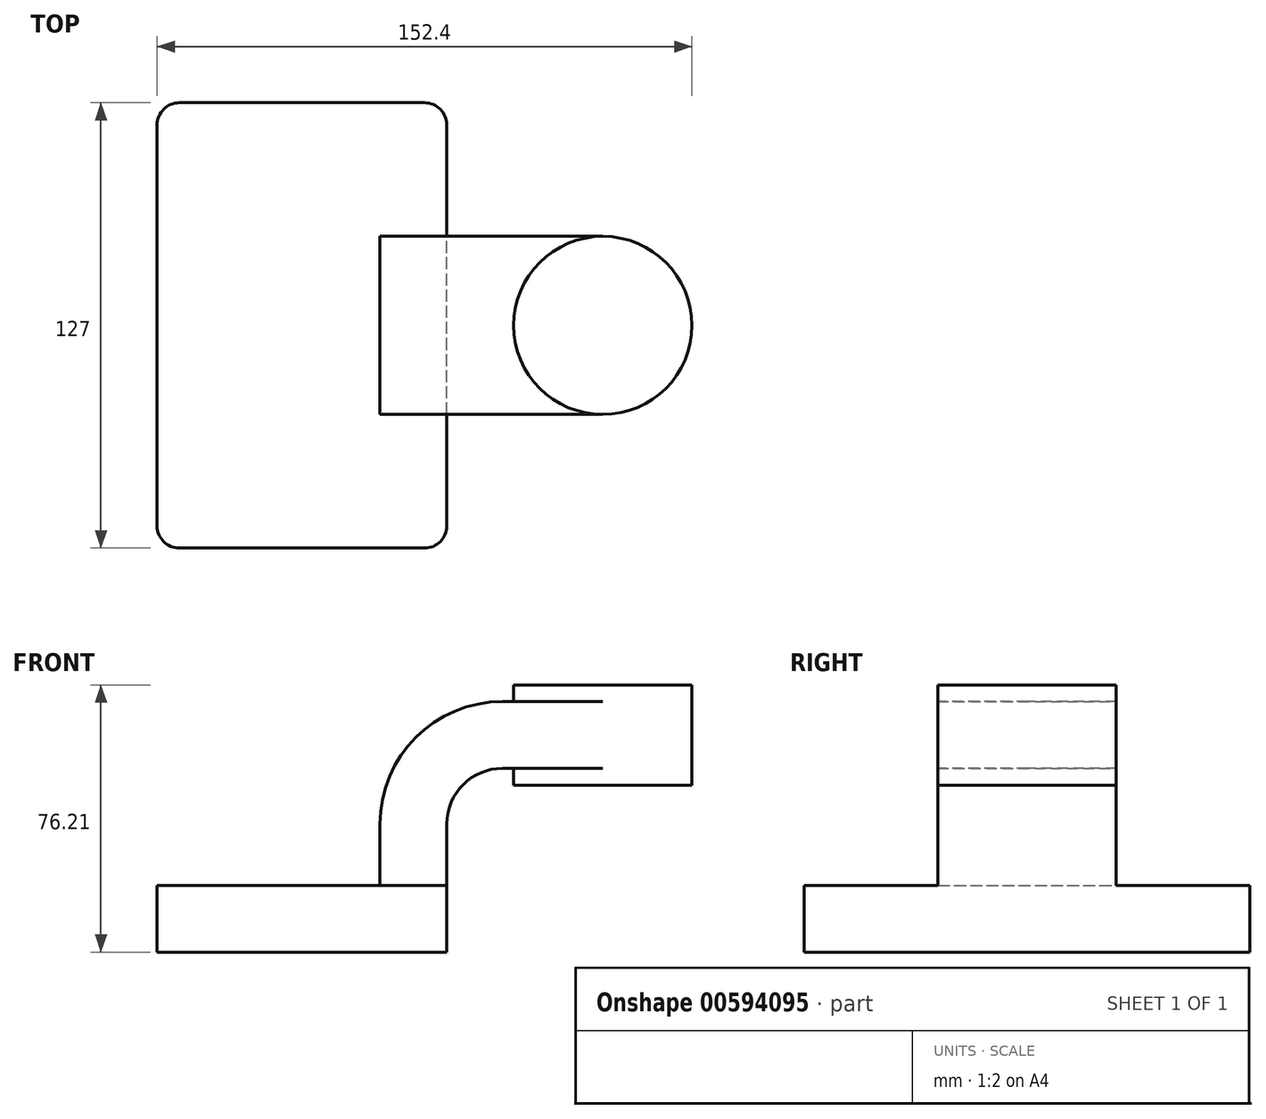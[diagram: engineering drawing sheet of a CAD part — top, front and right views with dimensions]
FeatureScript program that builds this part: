
annotation { "Feature Type Name" : "Feature", "Feature Type Description" : "" }
export const myFeature = defineFeature(function(context is Context, id is Id, definition is map)
    precondition{}
    {
        {
            var Q0;
            Q0=qCreatedBy(makeId("Front.planeOp"),FACE);
            var sketch = newSketch(context, id + "F0", { "sketchPlane" : qUnion([Q0])});
            skLineSegment(sketch, "E0.bottom", {"start": v(-41.28, -9.53) * mm, "end": v(41.28, -9.53) * mm});
            skLineSegment(sketch, "E0.top", {"start": v(-41.28, 9.53) * mm, "end": v(41.28, 9.53) * mm});
            skLineSegment(sketch, "E0.left", {"start": v(-41.28, -9.53) * mm, "end": v(-41.28, 9.53) * mm});
            skLineSegment(sketch, "E0.right", {"start": v(41.28, -9.53) * mm, "end": v(41.28, 9.53) * mm});
            skPoint(sketch, "E0.middle", {"position": v(0, 0) * mm});
            skLineSegment(sketch, "E1.bottom", {"start": v(60.32, 38.1) * mm, "end": v(111.12, 38.1) * mm});
            skLineSegment(sketch, "E1.top", {"start": v(60.32, 66.67) * mm, "end": v(111.12, 66.67) * mm});
            skLineSegment(sketch, "E1.left", {"start": v(60.32, 38.1) * mm, "end": v(60.32, 66.67) * mm});
            skLineSegment(sketch, "E1.right", {"start": v(111.12, 38.1) * mm, "end": v(111.12, 66.67) * mm});
            skPoint(sketch, "E1.middle", {"position": v(85.72, 52.39) * mm});
            skLineSegment(sketch, "E2", {"start": v(41.28, 9.52) * mm, "end": v(41.28, 27) * mm});
            skArc(sketch, "E3", {"start": v(41.27, 27) * mm, "mid": v(45.92, 38.23) * mm, "end": v(57.15, 42.88) * mm});
            skLineSegment(sketch, "E4", {"start": v(57.15, 42.88) * mm, "end": v(85.72, 42.88) * mm});
            skLineSegment(sketch, "E5.0", {"start": v(57.15, 61.93) * mm, "end": v(85.72, 61.93) * mm});
            skArc(sketch, "E5.1", {"start": v(22.22, 27) * mm, "mid": v(32.45, 51.7) * mm, "end": v(57.15, 61.93) * mm});
            skLineSegment(sketch, "E5.2", {"start": v(22.22, 9.52) * mm, "end": v(22.22, 27) * mm});
            skLineSegment(sketch, "E6", {"start": v(85.72, 38.1) * mm, "end": v(85.72, 66.67) * mm});
            skFitSpline(sketch, "E7", {"points": [v(-41.28, 9.53) * mm, v(57.15, 61.93) * mm], "startDerivative": vector(0.36, 92.94) * mm, "endDerivative": vector(178.9, -0.41) * mm});
            skSolve(sketch);
        }
        {
            var Q0;
            Q0=makeQuery(id+"F0.imprint","IMPRINT",FACE,{"disambiguationData":[TD([[makeQuery(id+"F0.imprint","IMPRINT",EDGE,{"derivedFrom":sQuery(id+"F0.wireOp",EDGE,"E0.bottom")}),1.0]])]});
            extrude(context, id + "F1", {"entities" : qUnion([Q0]), "endBound" : BoundingType.SYMMETRIC, "depth" : 127 * mm, "offsetDistance" : 25.4 * mm});
        }
        {
            var Q0;
            {var subQ1=sQuery(id+"F0.wireOp",EDGE,"E2");Q0=makeQuery(id+"F0.imprint","IMPRINT",FACE,{"disambiguationData":[TD([[makeQuery(id+"F0.imprint","IMPRINT",EDGE,{"derivedFrom":subQ1}),1.0]])]});}
            var Q1;
            {var subQ0=sQuery(id+"F0.wireOp",EDGE,"E4");var subQ1=sQuery(id+"F0.wireOp",EDGE,"E1.left");var subQ2=makeQuery(id+"F0.imprint","INTERSECT",VERTEX,{"derivedFrom":[subQ1,subQ0]});Q1=makeQuery(id+"F0.imprint","IMPRINT",FACE,{"disambiguationData":[TD([[makeQuery(id+"F0.imprint","IMPRINT",EDGE,{"disambiguationData":[TD([[subQ2,-1.0]])],"derivedFrom":subQ1}),-1.0]])]});}
            extrude(context, id + "F2", {"entities" : qUnion([Q0, Q1]), "operationType" : NewBodyOperationType.ADD, "endBound" : BoundingType.SYMMETRIC, "depth" : 50.8 * mm, "offsetDistance" : 25.4 * mm});
        }
        {
            var Q0;
            Q0=makeQuery(id+"F0.imprint","IMPRINT",FACE,{"disambiguationData":[TD([[makeQuery(id+"F0.imprint","IMPRINT",EDGE,{"derivedFrom":sQuery(id+"F0.wireOp",EDGE,"E5.1")}),1.0]])]});
            extrude(context, id + "F3", {"entities" : qUnion([Q0]), "operationType" : NewBodyOperationType.ADD, "endBound" : BoundingType.SYMMETRIC, "depth" : 15.88 * mm, "offsetDistance" : 25.4 * mm});
        }
        {
            var Q0;
            {var subQ0=sQuery(id+"F0.wireOp",EDGE,"E1.right");Q0=makeQuery(id+"F0.imprint","IMPRINT",FACE,{"disambiguationData":[TD([[makeQuery(id+"F0.imprint","IMPRINT",EDGE,{"derivedFrom":subQ0}),1.0]])]});}
            var Q1;
            Q1=sQuery(id+"F0.wireOp",EDGE,"E6");
            revolve(context, id + "F4", {"operationType" : NewBodyOperationType.ADD, "entities" : qUnion([Q0]), "axis" : qUnion([Q1]), "revolveType" : RevolveType.FULL});
        }
        {
            var Q0;
            Q0=makeQuery(id+"F1.opExtrude","CAP_EDGE",EDGE,{"disambiguationData":[OSD([sQuery(id+"F0.wireOp",EDGE,"E0.right")])],"isStart":false});
            var Q1;
            Q1=makeQuery(id+"F1.opExtrude","CAP_EDGE",EDGE,{"disambiguationData":[OSD([sQuery(id+"F0.wireOp",EDGE,"E0.left")])],"isStart":false});
            var Q2;
            Q2=makeQuery(id+"F1.opExtrude","CAP_EDGE",EDGE,{"disambiguationData":[OSD([sQuery(id+"F0.wireOp",EDGE,"E0.right")])],"isStart":true});
            var Q3;
            Q3=makeQuery(id+"F1.opExtrude","CAP_EDGE",EDGE,{"disambiguationData":[OSD([sQuery(id+"F0.wireOp",EDGE,"E0.left")])],"isStart":true});
            fillet(context, id + "F5", {"entities" : qUnion([Q0, Q1, Q2, Q3]), "radius" : 6.35 * mm, "tangentPropagation" : true, "allowEdgeOverflow" : false});
        }
    });
